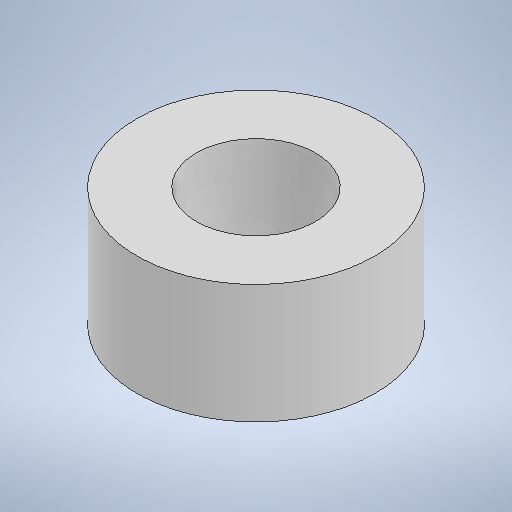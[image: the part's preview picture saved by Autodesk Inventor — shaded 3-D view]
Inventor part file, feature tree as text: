
AUTODESK INVENTOR PART (.ipt)
format: ipt  version: 2025.2 (Build 292293000, 293)  size: 195,072 bytes
history: native  units: mm
features: extrude x1, sketch x1
ambient origin geometry x8: Origin, YZ Plane, XZ Plane, XY Plane, X Axis, Y Axis, Z Axis, Center Point
bodies: Solid1 (feature_tree)
feature tree (2):
  extrude  "Extrusion1"  Depth=5.0mm
  sketch  "Sketch1"  dims[d0=10.0mm d1=5.0mm d2=5.0mm d3=0.0mm]
